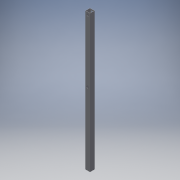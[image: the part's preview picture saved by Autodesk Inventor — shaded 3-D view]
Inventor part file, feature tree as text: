
AUTODESK INVENTOR PART (.ipt)
format: ipt  version: 2016 (Build 200138000, 138)  size: 110,080 bytes
history: native  units: in
note: dims shown in document units (in); Inventor stores cm internally (conversion verified against a paired STEP export)
features: extrude x2, sketch x2
ambient origin geometry x8: Origin, YZ Plane, XZ Plane, XY Plane, X Axis, Y Axis, Z Axis, Center Point
bodies: Solid1 (feature_tree)
feature tree (4):
  extrude  "Extrusion1"  Depth=1.0in
  extrude  "Extrusion2"  Depth=29.0in TaperAngle=0.0deg
  sketch  "Sketch1"  dims[d0=1.0in d1=1.0in]
  sketch  "Sketch2"  dims[d2=0.0625in d3=29.0in d4=0.0in d5=0.5in d6=0.5in d7=0.5in d8=13.7in d9=1.0in d10=0.0in d11=0.4761in]
